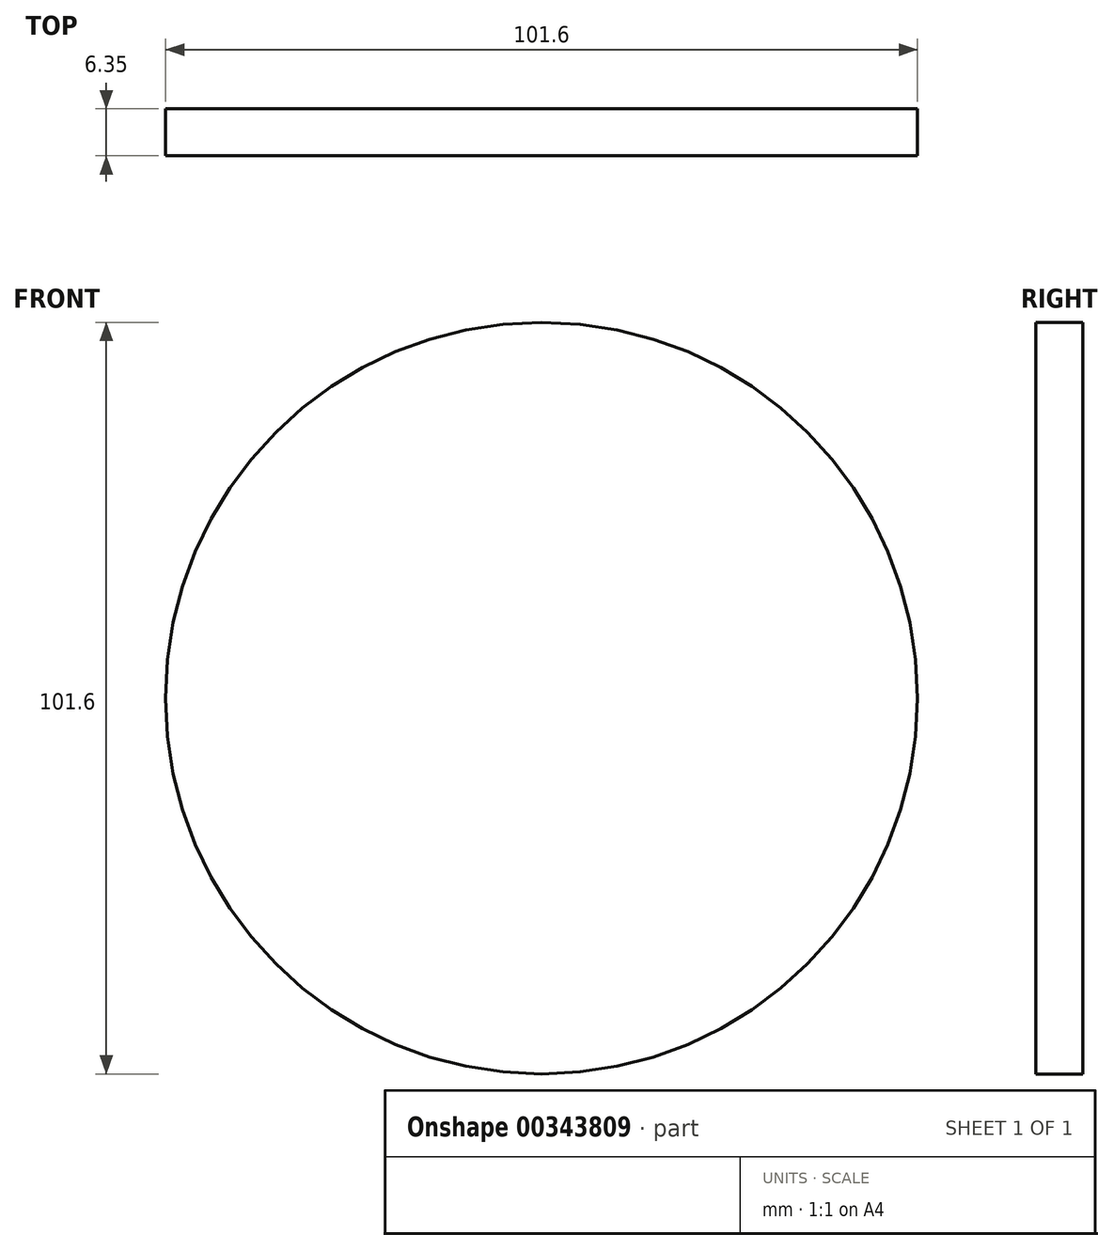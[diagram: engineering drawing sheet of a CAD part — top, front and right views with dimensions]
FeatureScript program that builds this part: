
annotation { "Feature Type Name" : "Feature", "Feature Type Description" : "" }
export const myFeature = defineFeature(function(context is Context, id is Id, definition is map)
    precondition{}
    {
        {
            var Q0;
            Q0=qCreatedBy(makeId("Front.planeOp"),FACE);
            var sketch = newSketch(context, id + "F0", { "sketchPlane" : qUnion([Q0])});
            skCircle(sketch, "E0", {"center": v(0, 0) * mm, "radius": 50.8 * mm});
            skSolve(sketch);
        }
        {
            var Q0;
            Q0 = qSketchRegion(id + "F0", true);
            extrude(context, id + "F1", {"entities" : qUnion([Q0]), "depth" : 6.35 * mm});
        }
    });
